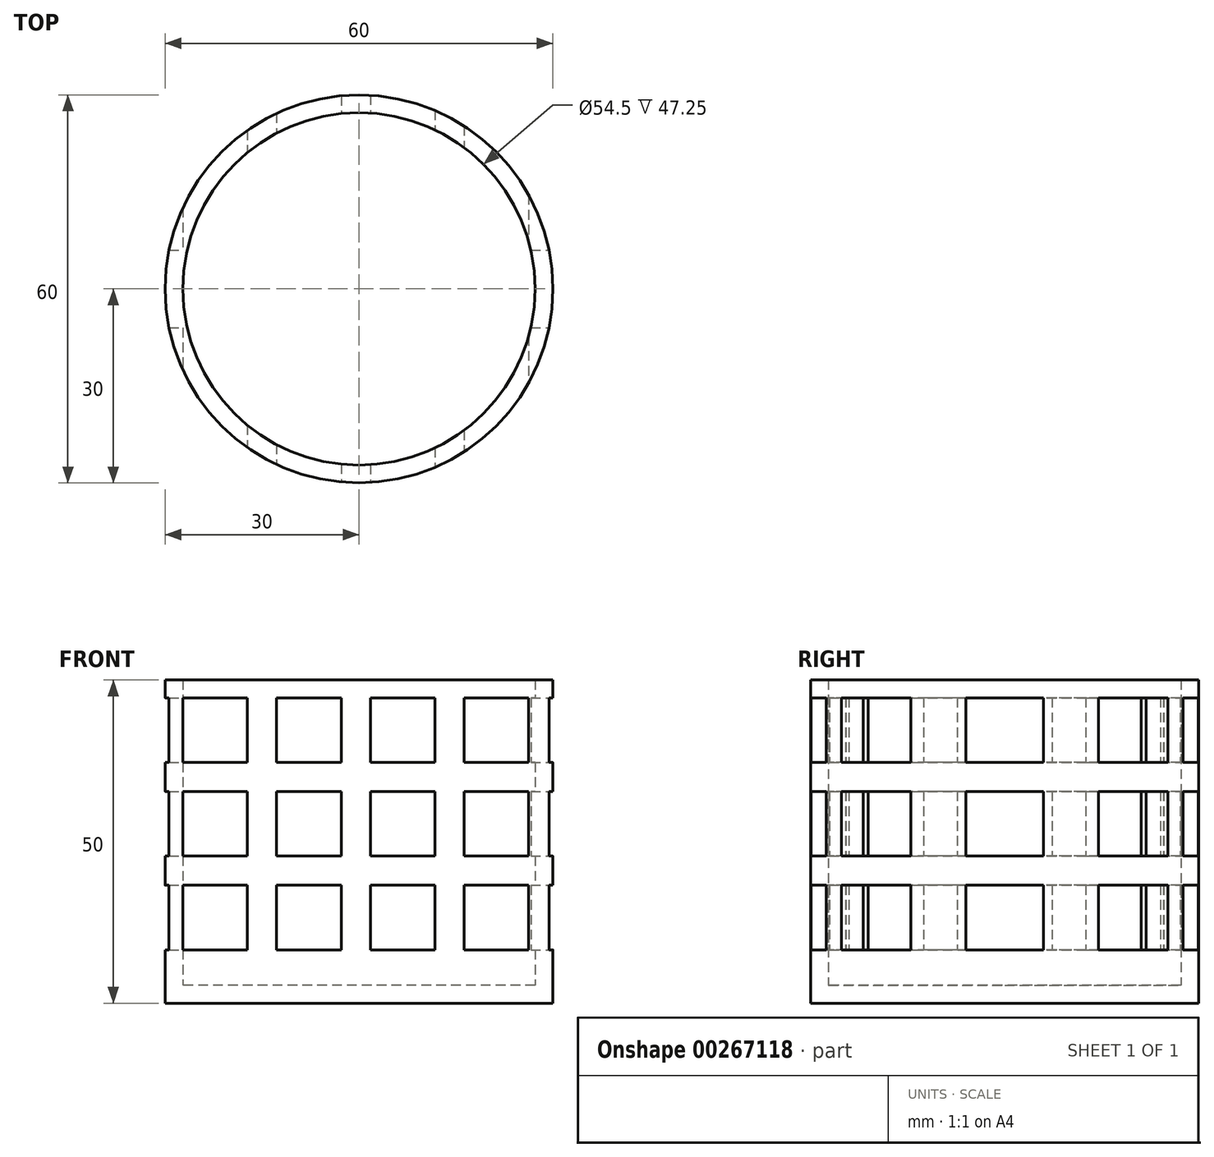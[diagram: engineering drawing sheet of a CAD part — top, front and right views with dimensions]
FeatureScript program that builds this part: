
annotation { "Feature Type Name" : "Feature", "Feature Type Description" : "" }
export const myFeature = defineFeature(function(context is Context, id is Id, definition is map)
    precondition{}
    {
        {
            var Q0;
            Q0=qCreatedBy(makeId("Top.planeOp"),FACE);
            var sketch = newSketch(context, id + "F0", { "sketchPlane" : qUnion([Q0])});
            skCircle(sketch, "E0", {"center": v(0, 0) * mm, "radius": 30 * mm});
            skSolve(sketch);
        }
        {
            var Q0;
            Q0=makeQuery(id+"F0.imprint","IMPRINT",FACE,{"disambiguationData":[TD([[makeQuery(id+"F0.imprint","IMPRINT",EDGE,{"derivedFrom":sQuery(id+"F0.wireOp",EDGE,"E0")}),1.0]])]});
            extrude(context, id + "F1", {"entities" : qUnion([Q0]), "depth" : 50 * mm});
        }
        {
            var Q0;
            Q0=makeQuery(id+"F1.opExtrude","CAP_FACE",FACE,{"disambiguationData":[OSD([sQuery(id+"F0.wireOp",EDGE,"E0")])],"isStart":false});
            shell(context, id + "F2", {"entities" : qUnion([Q0]), "thickness" : 2.75 * mm});
        }
        {
            var Q0;
            Q0=qCreatedBy(makeId("Front.planeOp"),FACE);
            var sketch = newSketch(context, id + "F3", { "sketchPlane" : qUnion([Q0])});
            skLineSegment(sketch, "E1", {"start": v(-30, 0) * mm, "end": v(-30, 50) * mm});
            skLineSegment(sketch, "E2.0", {"start": v(-30, 50) * mm, "end": v(30, 50) * mm});
            skLineSegment(sketch, "E3", {"start": v(30, 50) * mm, "end": v(30, 0) * mm});
            skLineSegment(sketch, "E4.bottom", {"start": v(-27.25, 47.25) * mm, "end": v(-17.25, 47.25) * mm});
            skLineSegment(sketch, "E4.top", {"start": v(-27.25, 37.25) * mm, "end": v(-17.25, 37.25) * mm});
            skLineSegment(sketch, "E4.left", {"start": v(-27.25, 47.25) * mm, "end": v(-27.25, 37.25) * mm});
            skLineSegment(sketch, "E4.right", {"start": v(-17.25, 47.25) * mm, "end": v(-17.25, 37.25) * mm});
            skLineSegment(sketch, "E5.0.1.0", {"start": v(-27.25, 32.75) * mm, "end": v(-17.25, 32.75) * mm});
            skLineSegment(sketch, "E5.0.1.1", {"start": v(-27.25, 32.75) * mm, "end": v(-27.25, 22.75) * mm});
            skLineSegment(sketch, "E5.0.1.2", {"start": v(-27.25, 22.75) * mm, "end": v(-17.25, 22.75) * mm});
            skLineSegment(sketch, "E5.0.1.3", {"start": v(-17.25, 32.75) * mm, "end": v(-17.25, 22.75) * mm});
            skLineSegment(sketch, "E5.0.2.0", {"start": v(-27.25, 18.25) * mm, "end": v(-17.25, 18.25) * mm});
            skLineSegment(sketch, "E5.0.2.1", {"start": v(-27.25, 18.25) * mm, "end": v(-27.25, 8.25) * mm});
            skLineSegment(sketch, "E5.0.2.2", {"start": v(-27.25, 8.25) * mm, "end": v(-17.25, 8.25) * mm});
            skLineSegment(sketch, "E5.0.2.3", {"start": v(-17.25, 18.25) * mm, "end": v(-17.25, 8.25) * mm});
            skLineSegment(sketch, "E5.1.0.0", {"start": v(-12.75, 47.25) * mm, "end": v(-2.75, 47.25) * mm});
            skLineSegment(sketch, "E5.1.0.1", {"start": v(-12.75, 47.25) * mm, "end": v(-12.75, 37.25) * mm});
            skLineSegment(sketch, "E5.1.0.2", {"start": v(-12.75, 37.25) * mm, "end": v(-2.75, 37.25) * mm});
            skLineSegment(sketch, "E5.1.0.3", {"start": v(-2.75, 47.25) * mm, "end": v(-2.75, 37.25) * mm});
            skLineSegment(sketch, "E5.1.1.0", {"start": v(-12.75, 32.75) * mm, "end": v(-2.75, 32.75) * mm});
            skLineSegment(sketch, "E5.1.1.1", {"start": v(-12.75, 32.75) * mm, "end": v(-12.75, 22.75) * mm});
            skLineSegment(sketch, "E5.1.1.2", {"start": v(-12.75, 22.75) * mm, "end": v(-2.75, 22.75) * mm});
            skLineSegment(sketch, "E5.1.1.3", {"start": v(-2.75, 32.75) * mm, "end": v(-2.75, 22.75) * mm});
            skLineSegment(sketch, "E5.1.2.0", {"start": v(-12.75, 18.25) * mm, "end": v(-2.75, 18.25) * mm});
            skLineSegment(sketch, "E5.1.2.1", {"start": v(-12.75, 18.25) * mm, "end": v(-12.75, 8.25) * mm});
            skLineSegment(sketch, "E5.1.2.2", {"start": v(-12.75, 8.25) * mm, "end": v(-2.75, 8.25) * mm});
            skLineSegment(sketch, "E5.1.2.3", {"start": v(-2.75, 18.25) * mm, "end": v(-2.75, 8.25) * mm});
            skLineSegment(sketch, "E5.2.0.0", {"start": v(1.75, 47.25) * mm, "end": v(11.75, 47.25) * mm});
            skLineSegment(sketch, "E5.2.0.1", {"start": v(1.75, 47.25) * mm, "end": v(1.75, 37.25) * mm});
            skLineSegment(sketch, "E5.2.0.2", {"start": v(1.75, 37.25) * mm, "end": v(11.75, 37.25) * mm});
            skLineSegment(sketch, "E5.2.0.3", {"start": v(11.75, 47.25) * mm, "end": v(11.75, 37.25) * mm});
            skLineSegment(sketch, "E5.2.1.0", {"start": v(1.75, 32.75) * mm, "end": v(11.75, 32.75) * mm});
            skLineSegment(sketch, "E5.2.1.1", {"start": v(1.75, 32.75) * mm, "end": v(1.75, 22.75) * mm});
            skLineSegment(sketch, "E5.2.1.2", {"start": v(1.75, 22.75) * mm, "end": v(11.75, 22.75) * mm});
            skLineSegment(sketch, "E5.2.1.3", {"start": v(11.75, 32.75) * mm, "end": v(11.75, 22.75) * mm});
            skLineSegment(sketch, "E5.2.2.0", {"start": v(1.75, 18.25) * mm, "end": v(11.75, 18.25) * mm});
            skLineSegment(sketch, "E5.2.2.1", {"start": v(1.75, 18.25) * mm, "end": v(1.75, 8.25) * mm});
            skLineSegment(sketch, "E5.2.2.2", {"start": v(1.75, 8.25) * mm, "end": v(11.75, 8.25) * mm});
            skLineSegment(sketch, "E5.2.2.3", {"start": v(11.75, 18.25) * mm, "end": v(11.75, 8.25) * mm});
            skLineSegment(sketch, "E5.3.0.0", {"start": v(16.25, 47.25) * mm, "end": v(26.25, 47.25) * mm});
            skLineSegment(sketch, "E5.3.0.1", {"start": v(16.25, 47.25) * mm, "end": v(16.25, 37.25) * mm});
            skLineSegment(sketch, "E5.3.0.2", {"start": v(16.25, 37.25) * mm, "end": v(26.25, 37.25) * mm});
            skLineSegment(sketch, "E5.3.0.3", {"start": v(26.25, 47.25) * mm, "end": v(26.25, 37.25) * mm});
            skLineSegment(sketch, "E5.3.1.0", {"start": v(16.25, 32.75) * mm, "end": v(26.25, 32.75) * mm});
            skLineSegment(sketch, "E5.3.1.1", {"start": v(16.25, 32.75) * mm, "end": v(16.25, 22.75) * mm});
            skLineSegment(sketch, "E5.3.1.2", {"start": v(16.25, 22.75) * mm, "end": v(26.25, 22.75) * mm});
            skLineSegment(sketch, "E5.3.1.3", {"start": v(26.25, 32.75) * mm, "end": v(26.25, 22.75) * mm});
            skLineSegment(sketch, "E5.3.2.0", {"start": v(16.25, 18.25) * mm, "end": v(26.25, 18.25) * mm});
            skLineSegment(sketch, "E5.3.2.1", {"start": v(16.25, 18.25) * mm, "end": v(16.25, 8.25) * mm});
            skLineSegment(sketch, "E5.3.2.2", {"start": v(16.25, 8.25) * mm, "end": v(26.25, 8.25) * mm});
            skLineSegment(sketch, "E5.3.2.3", {"start": v(26.25, 18.25) * mm, "end": v(26.25, 8.25) * mm});
            skLineSegment(sketch, "E5.direction1", {"start": v(-27.25, 47.25) * mm, "end": v(-12.75, 47.25) * mm, "construction": true});
            skLineSegment(sketch, "E5.direction2", {"start": v(-27.25, 47.25) * mm, "end": v(-27.25, 32.75) * mm, "construction": true});
            skSolve(sketch);
        }
        {
            var Q0;
            Q0 = qSketchRegion(id + "F3", true);
            extrude(context, id + "F4", {"entities" : qUnion([Q0]), "operationType" : NewBodyOperationType.REMOVE, "endBound" : BoundingType.SYMMETRIC, "oppositeDirection" : true, "depth" : 60 * mm});
        }
        {
            var Q0;
            Q0=qCreatedBy(makeId("Right.planeOp"),FACE);
            var sketch = newSketch(context, id + "F5", { "sketchPlane" : qUnion([Q0])});
            skLineSegment(sketch, "E6.0", {"start": v(-14.52, 8.25) * mm, "end": v(-25.22, 8.25) * mm});
            skLineSegment(sketch, "E7.0", {"start": v(-14.52, 18.25) * mm, "end": v(-25.22, 18.25) * mm});
            skLineSegment(sketch, "E8.bottom", {"start": v(-6, 8.25) * mm, "end": v(6, 8.25) * mm});
            skLineSegment(sketch, "E8.top", {"start": v(-6, 18.25) * mm, "end": v(6, 18.25) * mm});
            skLineSegment(sketch, "E8.left", {"start": v(-6, 8.25) * mm, "end": v(-6, 18.25) * mm});
            skLineSegment(sketch, "E8.right", {"start": v(6, 8.25) * mm, "end": v(6, 18.25) * mm});
            skLineSegment(sketch, "E9.0.1.0", {"start": v(6, 22.75) * mm, "end": v(6, 32.75) * mm});
            skLineSegment(sketch, "E9.0.1.1", {"start": v(-6, 32.75) * mm, "end": v(6, 32.75) * mm});
            skLineSegment(sketch, "E9.0.1.2", {"start": v(-6, 22.75) * mm, "end": v(-6, 32.75) * mm});
            skLineSegment(sketch, "E9.0.1.3", {"start": v(-6, 22.75) * mm, "end": v(6, 22.75) * mm});
            skLineSegment(sketch, "E9.0.2.0", {"start": v(6, 37.25) * mm, "end": v(6, 47.25) * mm});
            skLineSegment(sketch, "E9.0.2.1", {"start": v(-6, 47.25) * mm, "end": v(6, 47.25) * mm});
            skLineSegment(sketch, "E9.0.2.2", {"start": v(-6, 37.25) * mm, "end": v(-6, 47.25) * mm});
            skLineSegment(sketch, "E9.0.2.3", {"start": v(-6, 37.25) * mm, "end": v(6, 37.25) * mm});
            skLineSegment(sketch, "E9.direction1", {"start": v(6, 8.25) * mm, "end": v(31, 8.25) * mm, "construction": true});
            skLineSegment(sketch, "E9.direction2", {"start": v(6, 8.25) * mm, "end": v(6, 22.75) * mm, "construction": true});
            skSolve(sketch);
        }
        {
            var Q0;
            Q0 = qSketchRegion(id + "F5", true);
            var Q1;
            Q1 = qConstructionFilter(qBodyType(qCreatedBy(id + "F5" ,EDGE), BodyType.WIRE), ConstructionObject.NO);
            extrude(context, id + "F6", {"entities" : qUnion([Q0]), "operationType" : NewBodyOperationType.REMOVE, "surfaceEntities" : qUnion([Q1]), "endBound" : BoundingType.SYMMETRIC, "oppositeDirection" : true, "depth" : 100 * mm});
        }
    });
